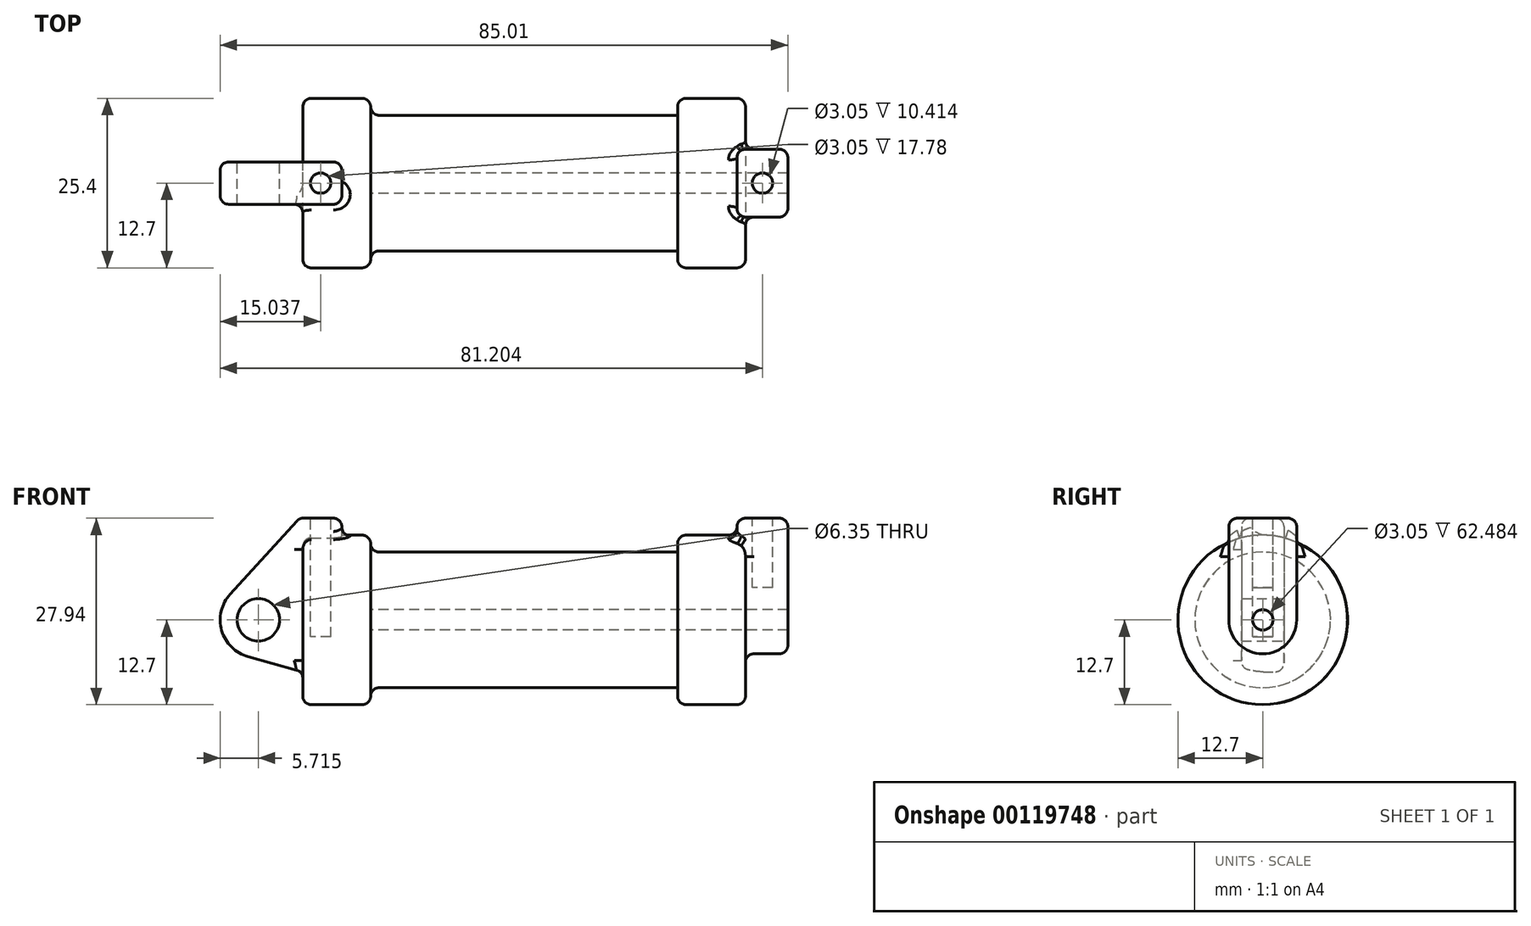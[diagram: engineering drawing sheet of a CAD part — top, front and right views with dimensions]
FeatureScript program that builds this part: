
annotation { "Feature Type Name" : "Feature", "Feature Type Description" : "" }
export const myFeature = defineFeature(function(context is Context, id is Id, definition is map)
    precondition{}
    {
        {
            var Q0;
            Q0=qCreatedBy(makeId("Front.planeOp"),FACE);
            var sketch = newSketch(context, id + "F0", { "sketchPlane" : qUnion([Q0])});
            skLineSegment(sketch, "E0", {"start": v(0, 0) * mm, "end": v(0, 12.7) * mm});
            skLineSegment(sketch, "E1", {"start": v(0, 12.7) * mm, "end": v(10.16, 12.7) * mm});
            skLineSegment(sketch, "E2", {"start": v(10.16, 12.7) * mm, "end": v(10.16, 10.16) * mm});
            skLineSegment(sketch, "E3", {"start": v(10.16, 10.16) * mm, "end": v(56.13, 10.16) * mm});
            skLineSegment(sketch, "E4", {"start": v(56.13, 10.16) * mm, "end": v(56.13, 12.7) * mm});
            skLineSegment(sketch, "E5", {"start": v(56.13, 12.7) * mm, "end": v(66.3, 12.7) * mm});
            skLineSegment(sketch, "E6", {"start": v(66.3, 12.7) * mm, "end": v(66.3, 0) * mm});
            skLineSegment(sketch, "E7", {"start": v(66.3, 0) * mm, "end": v(0, 0) * mm});
            skLineSegment(sketch, "E8", {"start": v(5.84, 15.24) * mm, "end": v(-0.5, 15.24) * mm});
            skLineSegment(sketch, "E9", {"start": v(-0.5, 15.24) * mm, "end": v(-10.88, 3.85) * mm});
            skLineSegment(sketch, "E10", {"start": v(0, 0) * mm, "end": v(-6.65, 0) * mm});
            skCircle(sketch, "E11", {"center": v(-6.65, 0) * mm, "radius": 5.72 * mm});
            skCircle(sketch, "E12", {"center": v(-6.65, 0) * mm, "radius": 3.18 * mm});
            skLineSegment(sketch, "E13", {"start": v(5.84, 15.24) * mm, "end": v(5.84, -9.4) * mm});
            skLineSegment(sketch, "E14", {"start": v(5.84, -9.4) * mm, "end": v(-8.18, -5.5) * mm});
            skSolve(sketch);
        }
        {
            var Q0;
            {var subQ0=sQuery(id+"F0.wireOp",EDGE,"E2");Q0=makeQuery(id+"F0.imprint","IMPRINT",FACE,{"disambiguationData":[TD([[makeQuery(id+"F0.imprint","IMPRINT",EDGE,{"derivedFrom":subQ0}),-1.0]])]});}
            var Q1;
            {var subQ0=sQuery(id+"F0.wireOp",EDGE,"E0");Q1=makeQuery(id+"F0.imprint","IMPRINT",FACE,{"disambiguationData":[TD([[makeQuery(id+"F0.imprint","IMPRINT",EDGE,{"derivedFrom":subQ0}),-1.0]])]});}
            var Q2;
            Q2=sQuery(id+"F0.wireOp",EDGE,"E7");
            revolve(context, id + "F1", {"entities" : qUnion([Q0, Q1]), "axis" : qUnion([Q2]), "revolveType" : RevolveType.FULL});
        }
        {
            var Q0;
            {var subQ4=sQuery(id+"F0.wireOp",EDGE,"E12");Q0=makeQuery(id+"F0.imprint","IMPRINT",FACE,{"disambiguationData":[TD([[makeQuery(id+"F0.imprint","IMPRINT",EDGE,{"derivedFrom":subQ4}),-1.0]])]});}
            var Q1;
            {var subQ3=sQuery(id+"F0.wireOp",EDGE,"E0");Q1=makeQuery(id+"F0.imprint","IMPRINT",FACE,{"disambiguationData":[TD([[makeQuery(id+"F0.imprint","IMPRINT",EDGE,{"derivedFrom":subQ3}),1.0]])]});}
            var Q2;
            {var subQ0=sQuery(id+"F0.wireOp",EDGE,"E14");Q2=makeQuery(id+"F0.imprint","IMPRINT",FACE,{"disambiguationData":[TD([[makeQuery(id+"F0.imprint","IMPRINT",EDGE,{"derivedFrom":subQ0}),-1.0]])]});}
            var Q3;
            {var subQ0=sQuery(id+"F0.wireOp",EDGE,"E0");Q3=makeQuery(id+"F0.imprint","IMPRINT",FACE,{"disambiguationData":[TD([[makeQuery(id+"F0.imprint","IMPRINT",EDGE,{"derivedFrom":subQ0}),-1.0]])]});}
            extrude(context, id + "F2", {"entities" : qUnion([Q0, Q1, Q2, Q3]), "operationType" : NewBodyOperationType.ADD, "endBound" : BoundingType.SYMMETRIC, "depth" : 6.35 * mm});
        }
        {
            var Q0;
            Q0=makeQuery(id+"F1.opRevolve","SWEPT_FACE",FACE,{"disambiguationData":[OSD([sQuery(id+"F0.wireOp",EDGE,"E6")])]});
            var sketch = newSketch(context, id + "F3", { "sketchPlane" : qUnion([Q0])});
            skCircle(sketch, "E15", {"center": v(0, 0) * mm, "radius": 1.52 * mm});
            skCircle(sketch, "E16", {"center": v(0, 0) * mm, "radius": 5.08 * mm});
            skLineSegment(sketch, "E17", {"start": v(-5.08, 0) * mm, "end": v(-5.08, 15.24) * mm});
            skLineSegment(sketch, "E18", {"start": v(-5.08, 15.24) * mm, "end": v(5.08, 15.24) * mm});
            skLineSegment(sketch, "E19", {"start": v(5.08, 15.24) * mm, "end": v(5.08, 0) * mm});
            skSolve(sketch);
        }
        {
            var Q0;
            Q0 = qSketchRegion(id + "F3", true);
            extrude(context, id + "F4", {"entities" : qUnion([Q0]), "operationType" : NewBodyOperationType.ADD, "depth" : 6.35 * mm, "hasSecondDirection" : true, "secondDirectionOppositeDirection" : true, "secondDirectionDepth" : 1.27 * mm});
        }
        {
            var Q0;
            Q0=makeQuery(id+"F4.boolean.opBoolean","SPLIT",FACE,{"disambiguationData":[TD([makeQuery(id+"F4.opExtrude","SWEPT_FACE",FACE,{"disambiguationData":[OSD([sQuery(id+"F3.wireOp",EDGE,"E15")])]})])],"derivedFrom":makeQuery(id+"F1.opRevolve","SWEPT_FACE",FACE,{"disambiguationData":[OSD([sQuery(id+"F0.wireOp",EDGE,"E6")])]})});
            var Q1;
            Q1=makeQuery(id+"F1.opRevolve","SWEPT_FACE",FACE,{"disambiguationData":[OSD([sQuery(id+"F0.wireOp",EDGE,"E2")])]});
            extrude(context, id + "F5", {"entities" : qUnion([Q0]), "operationType" : NewBodyOperationType.REMOVE, "endBound" : BoundingType.UP_TO_SURFACE, "oppositeDirection" : true, "endBoundEntityFace" : qUnion([Q1]), "depth" : 25.4 * mm});
        }
        {
            var Q0;
            Q0=makeQuery(id+"F4.opExtrude","SWEPT_FACE",FACE,{"disambiguationData":[OSD([sQuery(id+"F3.wireOp",EDGE,"E18")])]});
            var sketch = newSketch(context, id + "F6", { "sketchPlane" : qUnion([Q0])});
            skCircle(sketch, "E20", {"center": v(68.83, 0) * mm, "radius": 1.52 * mm});
            skLineSegment(sketch, "E21", {"start": v(65.02, -5.08) * mm, "end": v(72.64, 5.08) * mm, "construction": true});
            skSolve(sketch);
        }
        {
            var Q0;
            Q0=makeQuery(id+"F6.imprint","IMPRINT",FACE,{"disambiguationData":[TD([[makeQuery(id+"F6.imprint","IMPRINT",EDGE,{"derivedFrom":sQuery(id+"F6.wireOp",EDGE,"E20")}),1.0]])]});
            extrude(context, id + "F7", {"entities" : qUnion([Q0]), "operationType" : NewBodyOperationType.REMOVE, "oppositeDirection" : true, "depth" : 10.4 * mm});
        }
        {
            var Q0;
            Q0=makeQuery(id+"F2.opExtrude","SWEPT_FACE",FACE,{"disambiguationData":[OSD([sQuery(id+"F0.wireOp",EDGE,"E8")])]});
            var sketch = newSketch(context, id + "F8", { "sketchPlane" : qUnion([Q0])});
            skCircle(sketch, "E22", {"center": v(2.67, 0) * mm, "radius": 1.52 * mm});
            skLineSegment(sketch, "E23", {"start": v(-0.5, 3.18) * mm, "end": v(5.84, -3.18) * mm, "construction": true});
            skSolve(sketch);
        }
        {
            var Q0;
            Q0=makeQuery(id+"F8.imprint","IMPRINT",FACE,{"disambiguationData":[TD([[makeQuery(id+"F8.imprint","IMPRINT",EDGE,{"derivedFrom":sQuery(id+"F8.wireOp",EDGE,"E22")}),1.0]])]});
            var Q1;
            Q1=sQuery(id+"F8.wireOp",EDGE,"E22");
            extrude(context, id + "F9", {"entities" : qUnion([Q0]), "operationType" : NewBodyOperationType.REMOVE, "surfaceEntities" : qUnion([Q1]), "oppositeDirection" : true, "depth" : 17.78 * mm});
        }
        {
            var Q0;
            Q0=makeQuery(id+"F1.opRevolve","SWEPT_EDGE",EDGE,{"disambiguationData":[OSD([sQuery(id+"F0.wireOp",EDGE,"E2"),sQuery(id+"F0.wireOp",EDGE,"E3")])]});
            var Q1;
            Q1=makeQuery(id+"F1.opRevolve","SWEPT_EDGE",EDGE,{"disambiguationData":[OSD([sQuery(id+"F0.wireOp",EDGE,"E1"),sQuery(id+"F0.wireOp",EDGE,"E2")])]});
            var Q2;
            Q2=makeQuery(id+"F1.opRevolve","SWEPT_EDGE",EDGE,{"disambiguationData":[OSD([sQuery(id+"F0.wireOp",EDGE,"E0"),sQuery(id+"F0.wireOp",EDGE,"E1")])]});
            var Q3;
            Q3=makeQuery(id+"F1.opRevolve","SWEPT_EDGE",EDGE,{"disambiguationData":[OSD([sQuery(id+"F0.wireOp",EDGE,"E4"),sQuery(id+"F0.wireOp",EDGE,"E5")])]});
            var Q4;
            Q4=makeQuery(id+"F1.opRevolve","SWEPT_EDGE",EDGE,{"disambiguationData":[OSD([sQuery(id+"F0.wireOp",EDGE,"E5"),sQuery(id+"F0.wireOp",EDGE,"E6")])]});
            fillet(context, id + "F10", {"entities" : qUnion([Q0, Q1, Q2, Q3, Q4]), "radius" : 1.27 * mm, "tangentPropagation" : true, "allowEdgeOverflow" : false});
        }
        {
            var Q0;
            Q0=makeQuery(id+"F2.opExtrude","CAP_EDGE",EDGE,{"disambiguationData":[OSD([sQuery(id+"F0.wireOp",EDGE,"E11")])],"isStart":false});
            var Q1;
            Q1=makeQuery(id+"F2.boolean.opBoolean","INTERSECT",EDGE,{"derivedFrom":[makeQuery(id+"F1.opRevolve","SWEPT_FACE",FACE,{"disambiguationData":[OSD([sQuery(id+"F0.wireOp",EDGE,"E0")])]}),makeQuery(id+"F2.opExtrude","CAP_FACE",FACE,{"disambiguationData":[OSD([sQuery(id+"F0.wireOp",EDGE,"E8"),sQuery(id+"F0.wireOp",EDGE,"E9"),sQuery(id+"F0.wireOp",EDGE,"E11"),sQuery(id+"F0.wireOp",EDGE,"E12"),sQuery(id+"F0.wireOp",EDGE,"E13"),sQuery(id+"F0.wireOp",EDGE,"E14")])],"isStart":false})]});
            var Q2;
            Q2=makeQuery(id+"F2.opExtrude","CAP_EDGE",EDGE,{"disambiguationData":[OSD([sQuery(id+"F0.wireOp",EDGE,"E8")])],"isStart":false});
            var Q3;
            Q3=makeQuery(id+"F2.opExtrude","CAP_EDGE",EDGE,{"disambiguationData":[OSD([sQuery(id+"F0.wireOp",EDGE,"E13")])],"isStart":false});
            var Q4;
            Q4=makeQuery(id+"F2.opExtrude","SWEPT_EDGE",EDGE,{"disambiguationData":[OSD([sQuery(id+"F0.wireOp",EDGE,"E8"),sQuery(id+"F0.wireOp",EDGE,"E13")])]});
            var Q5;
            Q5=makeQuery(id+"F2.opExtrude","SWEPT_EDGE",EDGE,{"disambiguationData":[OSD([sQuery(id+"F0.wireOp",EDGE,"E8"),sQuery(id+"F0.wireOp",EDGE,"E9")])]});
            var Q6;
            Q6=makeQuery(id+"F2.opExtrude","CAP_EDGE",EDGE,{"disambiguationData":[OSD([sQuery(id+"F0.wireOp",EDGE,"E8")])],"isStart":true});
            var Q7;
            Q7=makeQuery(id+"F2.opExtrude","CAP_EDGE",EDGE,{"disambiguationData":[OSD([sQuery(id+"F0.wireOp",EDGE,"E13")])],"isStart":true});
            var Q8;
            Q8=makeQuery(id+"F2.opExtrude","CAP_EDGE",EDGE,{"disambiguationData":[OSD([sQuery(id+"F0.wireOp",EDGE,"E9")])],"isStart":true});
            fillet(context, id + "F11", {"entities" : qUnion([Q0, Q1, Q2, Q3, Q4, Q5, Q6, Q7, Q8]), "radius" : 1.27 * mm, "tangentPropagation" : true, "allowEdgeOverflow" : false});
        }
        {
            var Q0;
            Q0=makeQuery(id+"F4.opExtrude","CAP_EDGE",EDGE,{"disambiguationData":[OSD([sQuery(id+"F3.wireOp",EDGE,"E17")])],"isStart":false});
            var Q1;
            Q1=makeQuery(id+"F4.boolean.opBoolean","INTERSECT",EDGE,{"derivedFrom":[makeQuery(id+"F1.opRevolve","SWEPT_FACE",FACE,{"disambiguationData":[OSD([sQuery(id+"F0.wireOp",EDGE,"E6")])]}),makeQuery(id+"F4.opExtrude","SWEPT_FACE",FACE,{"disambiguationData":[OSD([sQuery(id+"F3.wireOp",EDGE,"E17")])]})]});
            var Q2;
            Q2=makeQuery(id+"F4.opExtrude","CAP_EDGE",EDGE,{"disambiguationData":[OSD([sQuery(id+"F3.wireOp",EDGE,"E17")])],"isStart":true});
            var Q3;
            Q3=makeQuery(id+"F4.opExtrude","SWEPT_EDGE",EDGE,{"disambiguationData":[OSD([sQuery(id+"F3.wireOp",EDGE,"E17"),sQuery(id+"F3.wireOp",EDGE,"E18")])]});
            var Q4;
            Q4=makeQuery(id+"F4.opExtrude","CAP_EDGE",EDGE,{"disambiguationData":[OSD([sQuery(id+"F3.wireOp",EDGE,"E18")])],"isStart":true});
            var Q5;
            Q5=makeQuery(id+"F4.opExtrude","CAP_EDGE",EDGE,{"disambiguationData":[OSD([sQuery(id+"F3.wireOp",EDGE,"E18")])],"isStart":false});
            var Q6;
            Q6=makeQuery(id+"F4.opExtrude","SWEPT_EDGE",EDGE,{"disambiguationData":[OSD([sQuery(id+"F3.wireOp",EDGE,"E18"),sQuery(id+"F3.wireOp",EDGE,"E19")])]});
            var Q7;
            Q7=makeQuery(id+"F10.opFillet","BLEND_EDGE",EDGE,{"blendedFrom":[makeQuery(id+"F1.opRevolve","SWEPT_EDGE",EDGE,{"disambiguationData":[OSD([sQuery(id+"F0.wireOp",EDGE,"E5"),sQuery(id+"F0.wireOp",EDGE,"E6")])]}),makeQuery(id+"F4.opExtrude","SWEPT_FACE",FACE,{"disambiguationData":[OSD([sQuery(id+"F3.wireOp",EDGE,"E17")])]})],"blendedInto":[makeQuery(id+"F4.opExtrude","SWEPT_FACE",FACE,{"disambiguationData":[OSD([sQuery(id+"F3.wireOp",EDGE,"E17")])]})]});
            var Q8;
            Q8=makeQuery(id+"F4.boolean.opBoolean","INTERSECT",EDGE,{"derivedFrom":[makeQuery(id+"F1.opRevolve","SWEPT_FACE",FACE,{"disambiguationData":[OSD([sQuery(id+"F0.wireOp",EDGE,"E6")])]}),makeQuery(id+"F4.opExtrude","SWEPT_FACE",FACE,{"disambiguationData":[OSD([sQuery(id+"F3.wireOp",EDGE,"E16")])]})]});
            var Q9;
            Q9=makeQuery(id+"F4.boolean.opBoolean","INTERSECT",EDGE,{"derivedFrom":[makeQuery(id+"F1.opRevolve","SWEPT_FACE",FACE,{"disambiguationData":[OSD([sQuery(id+"F0.wireOp",EDGE,"E6")])]}),makeQuery(id+"F4.opExtrude","SWEPT_FACE",FACE,{"disambiguationData":[OSD([sQuery(id+"F3.wireOp",EDGE,"E19")])]})]});
            var Q10;
            Q10=makeQuery(id+"F10.opFillet","BLEND_EDGE",EDGE,{"blendedFrom":[makeQuery(id+"F1.opRevolve","SWEPT_EDGE",EDGE,{"disambiguationData":[OSD([sQuery(id+"F0.wireOp",EDGE,"E5"),sQuery(id+"F0.wireOp",EDGE,"E6")])]}),makeQuery(id+"F4.opExtrude","SWEPT_FACE",FACE,{"disambiguationData":[OSD([sQuery(id+"F3.wireOp",EDGE,"E19")])]})],"blendedInto":[makeQuery(id+"F4.opExtrude","SWEPT_FACE",FACE,{"disambiguationData":[OSD([sQuery(id+"F3.wireOp",EDGE,"E19")])]})]});
            var Q11;
            Q11=makeQuery(id+"F4.opExtrude","CAP_EDGE",EDGE,{"disambiguationData":[OSD([sQuery(id+"F3.wireOp",EDGE,"E19")])],"isStart":true});
            var Q12;
            Q12=makeQuery(id+"F4.opExtrude","CAP_EDGE",EDGE,{"disambiguationData":[OSD([sQuery(id+"F3.wireOp",EDGE,"E19")])],"isStart":false});
            var Q13;
            Q13=makeQuery(id+"F4.opExtrude","CAP_EDGE",EDGE,{"disambiguationData":[OSD([sQuery(id+"F3.wireOp",EDGE,"E16")])],"isStart":false});
            var Q14;
            Q14=makeQuery(id+"F4.boolean.opBoolean","INTERSECT",EDGE,{"derivedFrom":[makeQuery(id+"F1.opRevolve","SWEPT_FACE",FACE,{"disambiguationData":[OSD([sQuery(id+"F0.wireOp",EDGE,"E5")])]}),makeQuery(id+"F4.opExtrude","CAP_FACE",FACE,{"disambiguationData":[OSD([sQuery(id+"F3.wireOp",EDGE,"E15"),sQuery(id+"F3.wireOp",EDGE,"E16"),sQuery(id+"F3.wireOp",EDGE,"E17"),sQuery(id+"F3.wireOp",EDGE,"E18"),sQuery(id+"F3.wireOp",EDGE,"E19")])],"isStart":true})]});
            fillet(context, id + "F12", {"entities" : qUnion([Q0, Q1, Q2, Q3, Q4, Q5, Q6, Q7, Q8, Q9, Q10, Q11, Q12, Q13, Q14]), "radius" : 1.27 * mm, "tangentPropagation" : true, "allowEdgeOverflow" : false});
        }
    });
